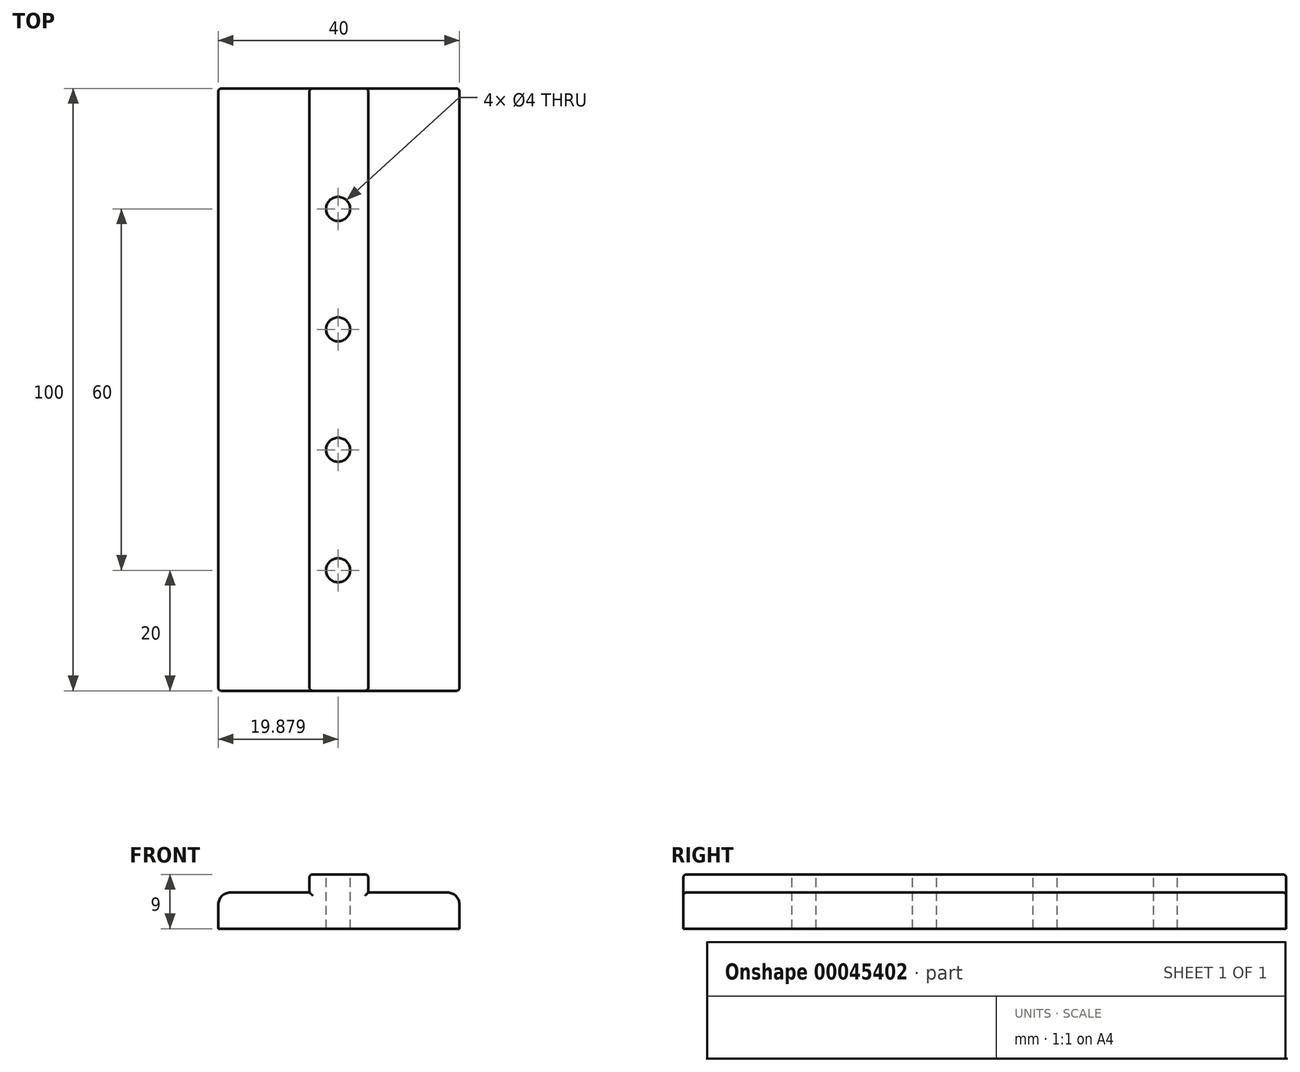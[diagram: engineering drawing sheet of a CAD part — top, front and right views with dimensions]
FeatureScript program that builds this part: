
annotation { "Feature Type Name" : "Feature", "Feature Type Description" : "" }
export const myFeature = defineFeature(function(context is Context, id is Id, definition is map)
    precondition{}
    {
        {
            var Q0;
            Q0=qCreatedBy(makeId("Front.planeOp"),FACE);
            var sketch = newSketch(context, id + "F0", { "sketchPlane" : qUnion([Q0])});
            skLineSegment(sketch, "E0", {"start": v(26.81, 0) * mm, "end": v(26.81, 4) * mm});
            skLineSegment(sketch, "E1", {"start": v(24.81, 6) * mm, "end": v(11.69, 6) * mm});
            skLineSegment(sketch, "E2", {"start": v(11.69, 6) * mm, "end": v(11.69, 8.5) * mm});
            skLineSegment(sketch, "E3", {"start": v(11.19, 9) * mm, "end": v(2.44, 9) * mm});
            skLineSegment(sketch, "E4", {"start": v(1.94, 8.5) * mm, "end": v(1.94, 6) * mm});
            skLineSegment(sketch, "E5", {"start": v(-11.19, 6) * mm, "end": v(1.94, 6) * mm});
            skLineSegment(sketch, "E6", {"start": v(-13.19, 4) * mm, "end": v(-13.19, 0) * mm});
            skLineSegment(sketch, "E7", {"start": v(-13.19, 0) * mm, "end": v(26.81, 0) * mm});
            skPoint(sketch, "E8.visualSharp", {"position": v(-13.19, 6) * mm});
            skArc(sketch, "E8.filletArc", {"start": v(-11.19, 6) * mm, "mid": v(-12.6, 5.41) * mm, "end": v(-13.19, 4) * mm});
            skPoint(sketch, "E9.visualSharp", {"position": v(26.81, 6) * mm});
            skArc(sketch, "E9.filletArc", {"start": v(26.81, 4) * mm, "mid": v(26.23, 5.41) * mm, "end": v(24.81, 6) * mm});
            skPoint(sketch, "E10.visualSharp", {"position": v(1.94, 9) * mm});
            skArc(sketch, "E10.filletArc", {"start": v(2.44, 9) * mm, "mid": v(2.09, 8.85) * mm, "end": v(1.94, 8.5) * mm});
            skPoint(sketch, "E11.visualSharp", {"position": v(11.69, 9) * mm});
            skArc(sketch, "E11.filletArc", {"start": v(11.69, 8.5) * mm, "mid": v(11.54, 8.85) * mm, "end": v(11.19, 9) * mm});
            skSolve(sketch);
        }
        {
            var Q0;
            Q0=makeQuery(id+"F0.imprint","IMPRINT",FACE,{"disambiguationData":[TD([[makeQuery(id+"F0.imprint","IMPRINT",EDGE,{"derivedFrom":sQuery(id+"F0.wireOp",EDGE,"E0")}),1.0]])]});
            extrude(context, id + "F1", {"entities" : qUnion([Q0]), "depth" : 100 * mm});
        }
        {
            var Q0;
            Q0=makeQuery(id+"F1.opExtrude","SWEPT_FACE",FACE,{"disambiguationData":[OSD([sQuery(id+"F0.wireOp",EDGE,"E3")])]});
            var sketch = newSketch(context, id + "F2", { "sketchPlane" : qUnion([Q0])});
            skCircle(sketch, "E12", {"center": v(6.69, -80) * mm, "radius": 2 * mm});
            skCircle(sketch, "E13", {"center": v(6.69, -60) * mm, "radius": 2 * mm});
            skCircle(sketch, "E14", {"center": v(6.69, -40) * mm, "radius": 2 * mm});
            skCircle(sketch, "E15", {"center": v(6.69, -20) * mm, "radius": 2 * mm});
            skSolve(sketch);
        }
        {
            var Q0;
            Q0=makeQuery(id+"F2.imprint","IMPRINT",FACE,{"disambiguationData":[TD([[makeQuery(id+"F2.imprint","IMPRINT",EDGE,{"derivedFrom":sQuery(id+"F2.wireOp",EDGE,"E12")}),1.0]])]});
            var Q1;
            Q1=makeQuery(id+"F2.imprint","IMPRINT",FACE,{"disambiguationData":[TD([[makeQuery(id+"F2.imprint","IMPRINT",EDGE,{"derivedFrom":sQuery(id+"F2.wireOp",EDGE,"E13")}),1.0]])]});
            var Q2;
            Q2=makeQuery(id+"F2.imprint","IMPRINT",FACE,{"disambiguationData":[TD([[makeQuery(id+"F2.imprint","IMPRINT",EDGE,{"derivedFrom":sQuery(id+"F2.wireOp",EDGE,"E14")}),1.0]])]});
            var Q3;
            Q3=makeQuery(id+"F2.imprint","IMPRINT",FACE,{"disambiguationData":[TD([[makeQuery(id+"F2.imprint","IMPRINT",EDGE,{"derivedFrom":sQuery(id+"F2.wireOp",EDGE,"E15")}),1.0]])]});
            extrude(context, id + "F3", {"entities" : qUnion([Q0, Q1, Q2, Q3]), "operationType" : NewBodyOperationType.REMOVE, "endBound" : BoundingType.UP_TO_NEXT, "oppositeDirection" : true, "depth" : 25 * mm});
        }
        {
            var Q0;
            Q0=makeQuery(id+"F1.opExtrude","CAP_EDGE",EDGE,{"disambiguationData":[OSD([sQuery(id+"F0.wireOp",EDGE,"E1")])],"isStart":false});
            var Q1;
            Q1=makeQuery(id+"F1.opExtrude","CAP_EDGE",EDGE,{"disambiguationData":[OSD([sQuery(id+"F0.wireOp",EDGE,"E3")])],"isStart":false});
            var Q2;
            Q2=makeQuery(id+"F1.opExtrude","CAP_EDGE",EDGE,{"disambiguationData":[OSD([sQuery(id+"F0.wireOp",EDGE,"E5")])],"isStart":false});
            var Q3;
            Q3=makeQuery(id+"F1.opExtrude","CAP_EDGE",EDGE,{"disambiguationData":[OSD([sQuery(id+"F0.wireOp",EDGE,"E2")])],"isStart":false});
            var Q4;
            Q4=makeQuery(id+"F1.opExtrude","CAP_EDGE",EDGE,{"disambiguationData":[OSD([sQuery(id+"F0.wireOp",EDGE,"E11.filletArc")])],"isStart":false});
            var Q5;
            Q5=makeQuery(id+"F1.opExtrude","CAP_EDGE",EDGE,{"disambiguationData":[OSD([sQuery(id+"F0.wireOp",EDGE,"E10.filletArc")])],"isStart":false});
            var Q6;
            Q6=makeQuery(id+"F1.opExtrude","CAP_EDGE",EDGE,{"disambiguationData":[OSD([sQuery(id+"F0.wireOp",EDGE,"E4")])],"isStart":false});
            var Q7;
            Q7=makeQuery(id+"F1.opExtrude","CAP_EDGE",EDGE,{"disambiguationData":[OSD([sQuery(id+"F0.wireOp",EDGE,"E6")])],"isStart":false});
            var Q8;
            Q8=makeQuery(id+"F1.opExtrude","CAP_EDGE",EDGE,{"disambiguationData":[OSD([sQuery(id+"F0.wireOp",EDGE,"E8.filletArc")])],"isStart":false});
            var Q9;
            Q9=makeQuery(id+"F1.opExtrude","CAP_EDGE",EDGE,{"disambiguationData":[OSD([sQuery(id+"F0.wireOp",EDGE,"E9.filletArc")])],"isStart":false});
            var Q10;
            Q10=makeQuery(id+"F1.opExtrude","CAP_EDGE",EDGE,{"disambiguationData":[OSD([sQuery(id+"F0.wireOp",EDGE,"E0")])],"isStart":false});
            var Q11;
            Q11=makeQuery(id+"F1.opExtrude","CAP_EDGE",EDGE,{"disambiguationData":[OSD([sQuery(id+"F0.wireOp",EDGE,"E6")])],"isStart":true});
            var Q12;
            Q12=makeQuery(id+"F1.opExtrude","CAP_EDGE",EDGE,{"disambiguationData":[OSD([sQuery(id+"F0.wireOp",EDGE,"E8.filletArc")])],"isStart":true});
            var Q13;
            Q13=makeQuery(id+"F1.opExtrude","CAP_EDGE",EDGE,{"disambiguationData":[OSD([sQuery(id+"F0.wireOp",EDGE,"E4")])],"isStart":true});
            var Q14;
            Q14=makeQuery(id+"F1.opExtrude","CAP_EDGE",EDGE,{"disambiguationData":[OSD([sQuery(id+"F0.wireOp",EDGE,"E10.filletArc")])],"isStart":true});
            var Q15;
            Q15=makeQuery(id+"F1.opExtrude","CAP_EDGE",EDGE,{"disambiguationData":[OSD([sQuery(id+"F0.wireOp",EDGE,"E3")])],"isStart":true});
            var Q16;
            Q16=makeQuery(id+"F1.opExtrude","CAP_EDGE",EDGE,{"disambiguationData":[OSD([sQuery(id+"F0.wireOp",EDGE,"E1")])],"isStart":true});
            var Q17;
            Q17=makeQuery(id+"F1.opExtrude","CAP_EDGE",EDGE,{"disambiguationData":[OSD([sQuery(id+"F0.wireOp",EDGE,"E9.filletArc")])],"isStart":true});
            fillet(context, id + "F4", {"entities" : qUnion([Q0, Q1, Q2, Q3, Q4, Q5, Q6, Q7, Q8, Q9, Q10, Q11, Q12, Q13, Q14, Q15, Q16, Q17]), "radius" : .5 * mm, "tangentPropagation" : true, "allowEdgeOverflow" : false});
        }
    });
